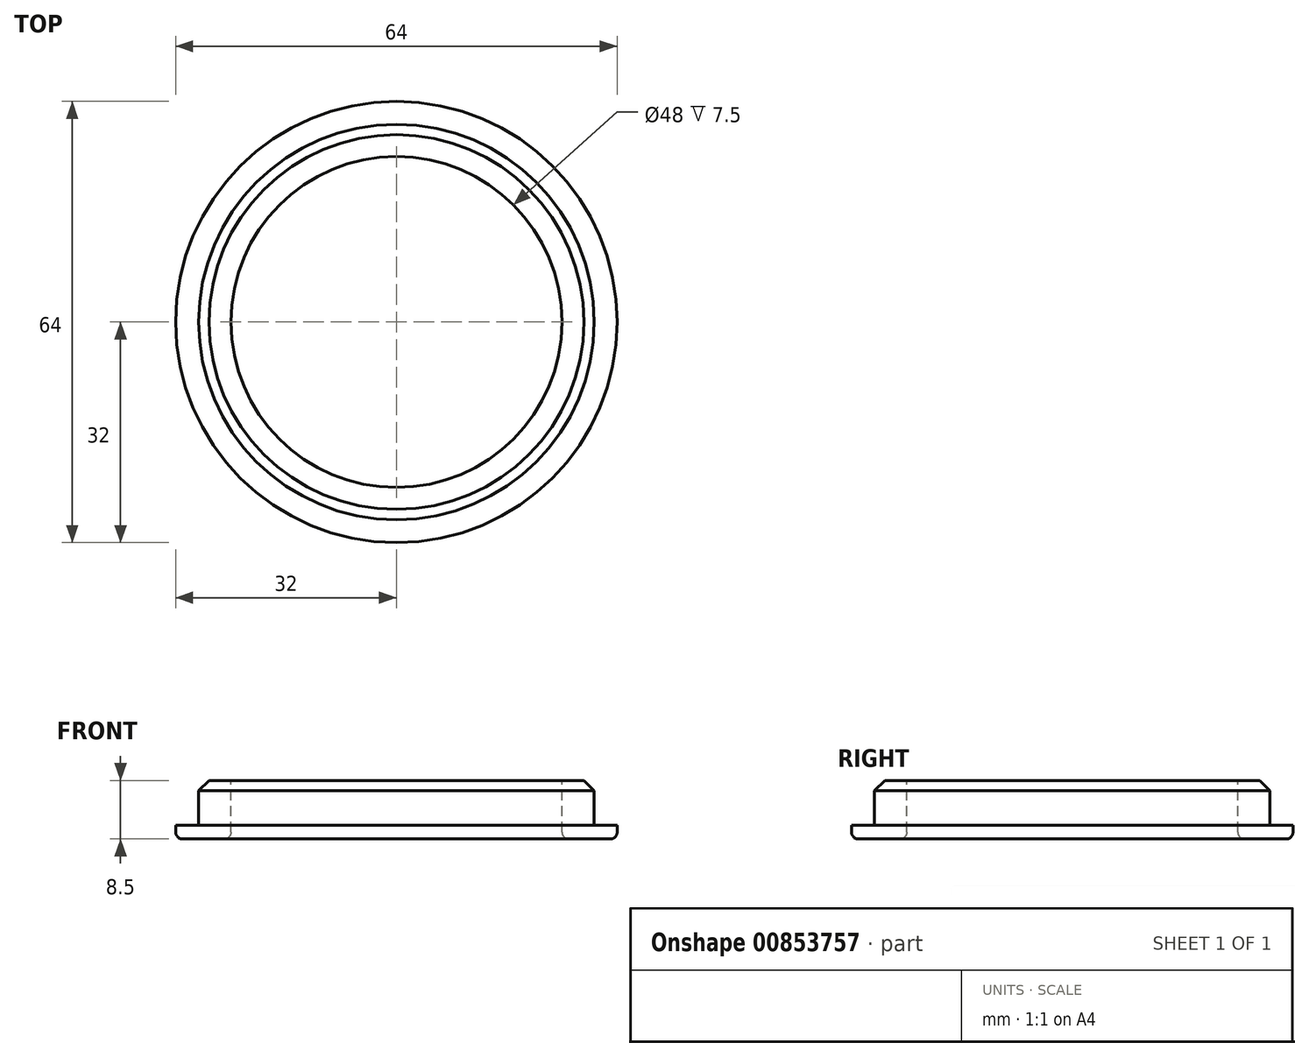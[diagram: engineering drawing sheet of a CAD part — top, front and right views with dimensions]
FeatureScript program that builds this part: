
annotation { "Feature Type Name" : "Feature", "Feature Type Description" : "" }
export const myFeature = defineFeature(function(context is Context, id is Id, definition is map)
    precondition{}
    {
        {
            var Q0;
            Q0=qCreatedBy(makeId("Top.planeOp"),FACE);
            var sketch = newSketch(context, id + "F0", { "sketchPlane" : qUnion([Q0])});
            skCircle(sketch, "E0", {"center": v(0, 0) * mm, "radius": 32 * mm});
            skSolve(sketch);
        }
        {
            var Q0;
            Q0=qCreatedBy(makeId("Top.planeOp"),FACE);
            var sketch = newSketch(context, id + "F1", { "sketchPlane" : qUnion([Q0])});
            skCircle(sketch, "E1", {"center": v(0, 0) * mm, "radius": 28.68 * mm});
            skSolve(sketch);
        }
        {
            var Q0;
            Q0=qCreatedBy(makeId("Top.planeOp"),FACE);
            var sketch = newSketch(context, id + "F2", { "sketchPlane" : qUnion([Q0])});
            skCircle(sketch, "E2", {"center": v(0, 0) * mm, "radius": 24 * mm});
            skSolve(sketch);
        }
        {
            var Q0;
            Q0 = qSketchRegion(id + "F0", true);
            extrude(context, id + "F3", {"entities" : qUnion([Q0]), "oppositeDirection" : true, "depth" : 2 * mm, "offsetDistance" : 25 * mm});
        }
        {
            var Q0;
            Q0 = qSketchRegion(id + "F1", true);
            extrude(context, id + "F4", {"entities" : qUnion([Q0]), "operationType" : NewBodyOperationType.ADD, "depth" : 6.5 * mm, "offsetDistance" : 25 * mm});
        }
        {
            var Q0;
            Q0 = qSketchRegion(id + "F2", true);
            extrude(context, id + "F5", {"entities" : qUnion([Q0]), "operationType" : NewBodyOperationType.REMOVE, "endBound" : BoundingType.SYMMETRIC, "oppositeDirection" : true, "depth" : 20 * mm, "offsetDistance" : 25 * mm});
        }
        {
            var Q0;
            Q0=makeQuery(id+"F4.opExtrude","CAP_EDGE",EDGE,{"disambiguationData":[OSD([sQuery(id+"F1.wireOp",EDGE,"E1")])],"isStart":false});
            chamfer(context, id + "F6", {"entities" : qUnion([Q0]), "width" : 1.5 * mm, "tangentPropagation" : true});
        }
        {
            var Q0;
            Q0=makeQuery(id+"F5.boolean.opBoolean","INTERSECT",EDGE,{"derivedFrom":[makeQuery(id+"F3.opExtrude","CAP_FACE",FACE,{"disambiguationData":[OSD([sQuery(id+"F0.wireOp",EDGE,"E0")])],"isStart":false}),makeQuery(id+"F5.opExtrude","SWEPT_FACE",FACE,{"disambiguationData":[OSD([sQuery(id+"F2.wireOp",EDGE,"E2")])]})]});
            var Q1;
            Q1=makeQuery(id+"F3.opExtrude","CAP_EDGE",EDGE,{"disambiguationData":[OSD([sQuery(id+"F0.wireOp",EDGE,"E0")])],"isStart":false});
            fillet(context, id + "F7", {"entities" : qUnion([Q0, Q1]), "radius" : 1 * mm, "tangentPropagation" : true, "allowEdgeOverflow" : false});
        }
    });
